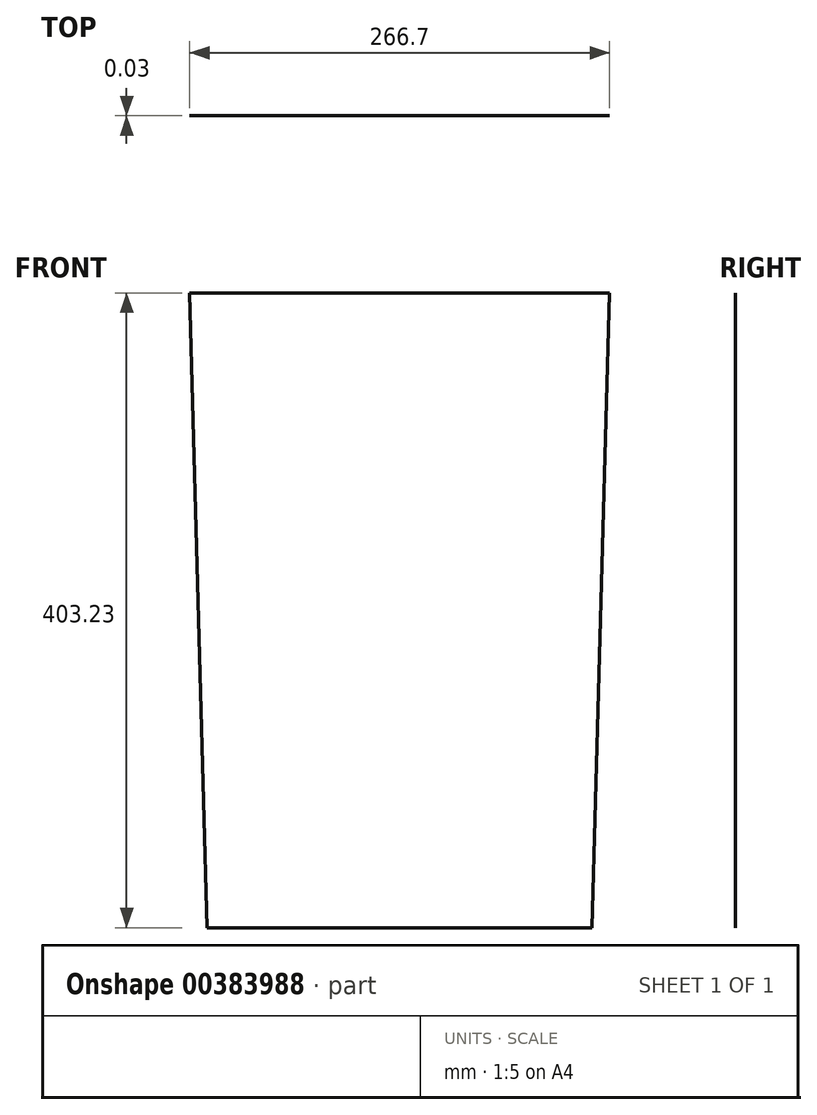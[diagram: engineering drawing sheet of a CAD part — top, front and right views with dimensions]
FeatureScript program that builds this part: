
annotation { "Feature Type Name" : "Feature", "Feature Type Description" : "" }
export const myFeature = defineFeature(function(context is Context, id is Id, definition is map)
    precondition{}
    {
        {
            var Q0;
            Q0=qCreatedBy(makeId("Front.planeOp"),FACE);
            var sketch = newSketch(context, id + "F0", { "sketchPlane" : qUnion([Q0])});
            skLineSegment(sketch, "E0", {"start": v(0, 0) * mm, "end": v(0, -403.23) * mm, "construction": true});
            skLineSegment(sketch, "E1", {"start": v(0, 0) * mm, "end": v(133.35, 0) * mm});
            skLineSegment(sketch, "E2", {"start": v(133.35, 0) * mm, "end": v(122.24, -403.23) * mm});
            skLineSegment(sketch, "E3", {"start": v(122.24, -403.23) * mm, "end": v(0, -403.23) * mm});
            skLineSegment(sketch, "E4", {"start": v(0, -403.23) * mm, "end": v(-122.24, -403.23) * mm});
            skLineSegment(sketch, "E5", {"start": v(-122.24, -403.23) * mm, "end": v(-133.35, 0) * mm});
            skLineSegment(sketch, "E6", {"start": v(-133.35, 0) * mm, "end": v(0, 0) * mm});
            skLineSegment(sketch, "E7", {"start": v(90.49, 0) * mm, "end": v(90.49, -403.23) * mm, "construction": true});
            skLineSegment(sketch, "E8", {"start": v(-90.49, 0) * mm, "end": v(-90.49, -403.23) * mm, "construction": true});
            skSolve(sketch);
        }
        {
            var Q0;
            Q0=makeQuery(id+"F0.imprint","IMPRINT",FACE,{"disambiguationData":[TD([[makeQuery(id+"F0.imprint","IMPRINT",EDGE,{"derivedFrom":sQuery(id+"F0.wireOp",EDGE,"E1")}),-1.0]])]});
            extrude(context, id + "F1", {"entities" : qUnion([Q0]), "depth" : 3 / 101.6 * mm, "offsetDistance" : 25.4 * mm});
        }
    });
